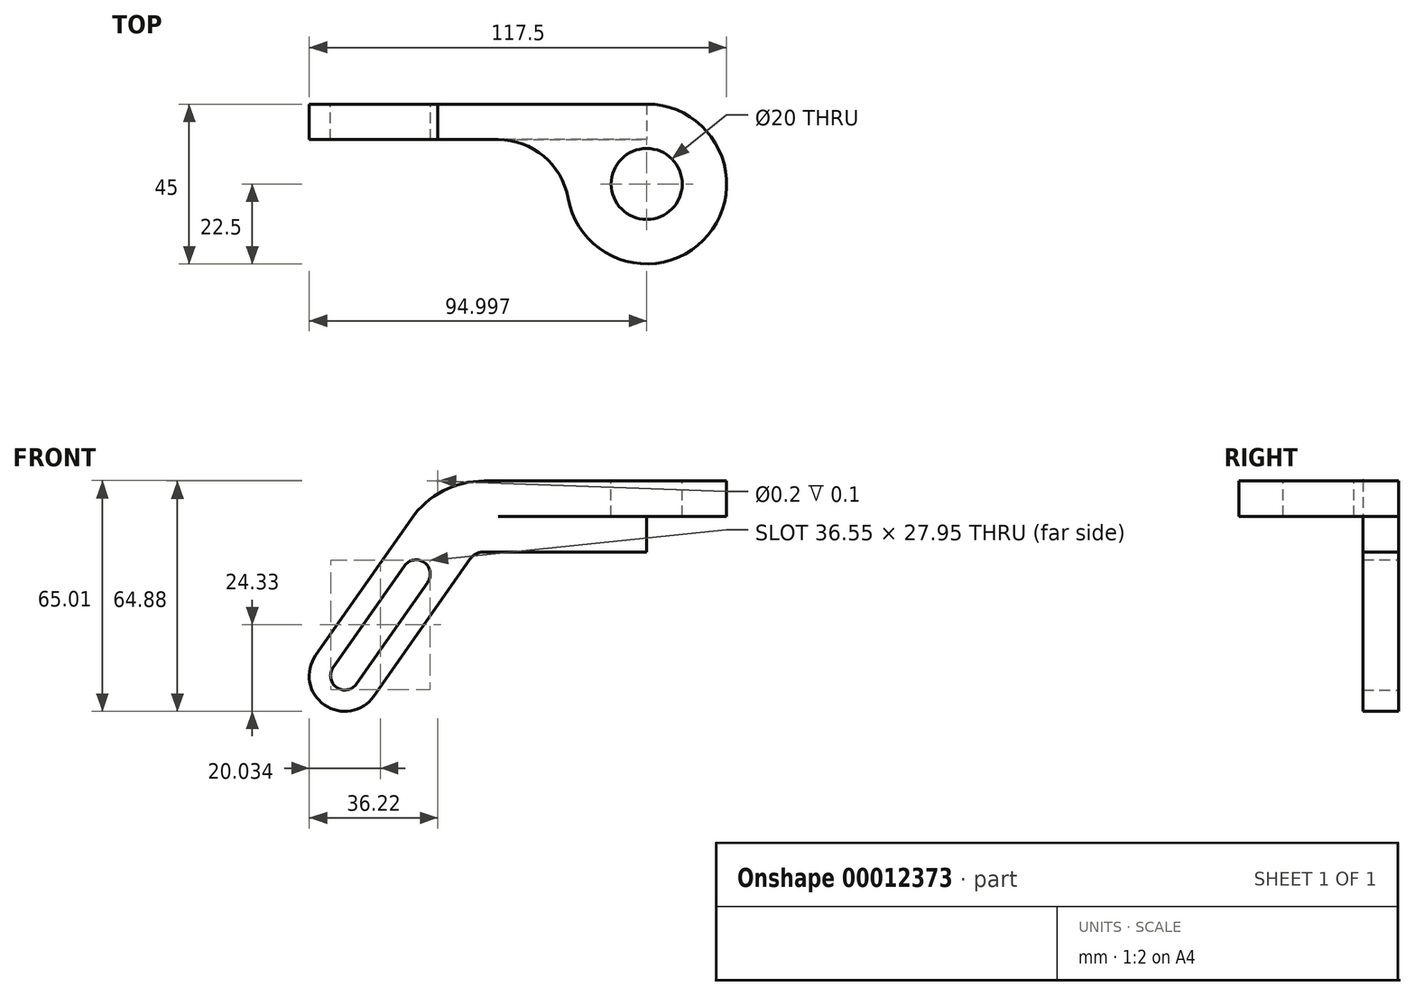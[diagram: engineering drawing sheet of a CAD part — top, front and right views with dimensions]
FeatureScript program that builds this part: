
annotation { "Feature Type Name" : "Feature", "Feature Type Description" : "" }
export const myFeature = defineFeature(function(context is Context, id is Id, definition is map)
    precondition{}
    {
        {
            var Q0;
            Q0=qCreatedBy(makeId("Front.planeOp"),FACE);
            var sketch = newSketch(context, id + "F0", { "sketchPlane" : qUnion([Q0])});
            skLineSegment(sketch, "E0", {"start": v(13.01, 0) * mm, "end": v(58.78, 0) * mm});
            skLineSegment(sketch, "E1", {"start": v(-7.46, -10.66) * mm, "end": v(-34.41, -49.15) * mm});
            skLineSegment(sketch, "E2.0", {"start": v(8.92, -22.13) * mm, "end": v(-18.03, -60.62) * mm});
            skArc(sketch, "E3", {"start": v(-18.03, -60.62) * mm, "mid": v(-31.96, -63.08) * mm, "end": v(-34.41, -49.15) * mm});
            skLineSegment(sketch, "E4.0", {"start": v(13.01, -20) * mm, "end": v(58.78, -20) * mm});
            skLineSegment(sketch, "E5", {"start": v(58.78, 0) * mm, "end": v(58.78, -20) * mm});
            skPoint(sketch, "E6.visualSharp", {"position": v(0, 0) * mm});
            skArc(sketch, "E6.filletArc", {"start": v(13.01, 0) * mm, "mid": v(1.47, -2.82) * mm, "end": v(-7.46, -10.66) * mm});
            skArc(sketch, "E7.filletArc", {"start": v(13.01, -20) * mm, "mid": v(10.7, -20.56) * mm, "end": v(8.92, -22.13) * mm});
            skLineSegment(sketch, "E8", {"start": v(0, 0) * mm, "end": v(-4.4, -6.28) * mm, "construction": true});
            skLineSegment(sketch, "E9", {"start": v(0, 0) * mm, "end": v(6.9, 0) * mm, "construction": true});
            skCircle(sketch, "E10", {"center": v(0, 0) * mm, "radius": 0 * mm});
            skSolve(sketch);
        }
        {
            var Q0;
            Q0 = qSketchRegion(id + "F0", true);
            extrude(context, id + "F1", {"entities" : qUnion([Q0]), "depth" : 10 * mm});
        }
        {
            var Q0;
            Q0=makeQuery(id+"F1.opExtrude","SWEPT_FACE",FACE,{"disambiguationData":[OSD([sQuery(id+"F0.wireOp",EDGE,"E0")])]});
            var sketch = newSketch(context, id + "F2", { "sketchPlane" : qUnion([Q0])});
            skCircle(sketch, "E11", {"center": v(58.78, -22.5) * mm, "radius": 22.5 * mm});
            skSolve(sketch);
        }
        {
            var Q0;
            Q0 = qSketchRegion(id + "F2", true);
            extrude(context, id + "F3", {"entities" : qUnion([Q0]), "operationType" : NewBodyOperationType.ADD, "oppositeDirection" : true, "depth" : 10 * mm});
        }
        {
            var Q0;
            Q0=makeQuery(id+"F3.boolean.opBoolean","INTERSECT",EDGE,{"derivedFrom":[makeQuery(id+"F1.opExtrude","CAP_FACE",FACE,{"disambiguationData":[OSD([sQuery(id+"F0.wireOp",EDGE,"E0"),sQuery(id+"F0.wireOp",EDGE,"E1"),sQuery(id+"F0.wireOp",EDGE,"E2.0"),sQuery(id+"F0.wireOp",EDGE,"E3"),sQuery(id+"F0.wireOp",EDGE,"E4.0"),sQuery(id+"F0.wireOp",EDGE,"E5"),sQuery(id+"F0.wireOp",EDGE,"E6.filletArc"),sQuery(id+"F0.wireOp",EDGE,"E7.filletArc")])],"isStart":false}),makeQuery(id+"F3.opExtrude","SWEPT_FACE",FACE,{"disambiguationData":[OSD([sQuery(id+"F2.wireOp",EDGE,"E11")])]})]});
            fillet(context, id + "F4", {"entities" : qUnion([Q0]), "radius" : 20 * mm, "tangentPropagation" : true, "allowEdgeOverflow" : false});
        }
        {
            var Q0;
            Q0=makeQuery(id+"F1.opExtrude","CAP_FACE",FACE,{"disambiguationData":[OSD([sQuery(id+"F0.wireOp",EDGE,"E0"),sQuery(id+"F0.wireOp",EDGE,"E1"),sQuery(id+"F0.wireOp",EDGE,"E2.0"),sQuery(id+"F0.wireOp",EDGE,"E3"),sQuery(id+"F0.wireOp",EDGE,"E4.0"),sQuery(id+"F0.wireOp",EDGE,"E5"),sQuery(id+"F0.wireOp",EDGE,"E6.filletArc"),sQuery(id+"F0.wireOp",EDGE,"E7.filletArc")])],"isStart":true});
            var sketch = newSketch(context, id + "F5", { "sketchPlane" : qUnion([Q0])});
            skArc(sketch, "E12", {"start": v(22.95, -57.18) * mm, "mid": v(28.52, -58.16) * mm, "end": v(29.5, -52.6) * mm});
            skLineSegment(sketch, "E13", {"start": v(26.22, -54.88) * mm, "end": v(2.44, -20.92) * mm, "construction": true});
            skArc(sketch, "E14", {"start": v(9.42, -23.92) * mm, "mid": v(3.85, -22.94) * mm, "end": v(2.87, -28.5) * mm});
            skLineSegment(sketch, "E15", {"start": v(22.95, -57.18) * mm, "end": v(2.87, -28.5) * mm});
            skLineSegment(sketch, "E16.0", {"start": v(29.5, -52.6) * mm, "end": v(9.42, -23.92) * mm});
            skSolve(sketch);
        }
        {
            var Q0;
            Q0 = qSketchRegion(id + "F5", true);
            extrude(context, id + "F6", {"entities" : qUnion([Q0]), "operationType" : NewBodyOperationType.REMOVE, "endBound" : BoundingType.THROUGH_ALL, "oppositeDirection" : true, "depth" : 25 * mm});
        }
        {
            var Q0;
            Q0=makeQuery(id+"F3.boolean.opBoolean","MERGE",FACE,{"derivedFrom":[makeQuery(id+"F1.opExtrude","SWEPT_FACE",FACE,{"disambiguationData":[OSD([sQuery(id+"F0.wireOp",EDGE,"E0")])]}),makeQuery(id+"F3.opExtrude","CAP_FACE",FACE,{"disambiguationData":[OSD([sQuery(id+"F2.wireOp",EDGE,"E11")])],"isStart":true})]});
            var sketch = newSketch(context, id + "F7", { "sketchPlane" : qUnion([Q0])});
            skCircle(sketch, "E17", {"center": v(58.78, -22.5) * mm, "radius": 10 * mm});
            skSolve(sketch);
        }
        {
            var Q0;
            Q0 = qSketchRegion(id + "F7", true);
            extrude(context, id + "F8", {"entities" : qUnion([Q0]), "operationType" : NewBodyOperationType.REMOVE, "endBound" : BoundingType.THROUGH_ALL, "oppositeDirection" : true, "depth" : 25 * mm});
        }
        {
            var Q0;
            Q0=makeQuery(id+"F1.opExtrude","CAP_FACE",FACE,{"disambiguationData":[OSD([sQuery(id+"F0.wireOp",EDGE,"E0"),sQuery(id+"F0.wireOp",EDGE,"E1"),sQuery(id+"F0.wireOp",EDGE,"E2.0"),sQuery(id+"F0.wireOp",EDGE,"E3"),sQuery(id+"F0.wireOp",EDGE,"E4.0"),sQuery(id+"F0.wireOp",EDGE,"E5"),sQuery(id+"F0.wireOp",EDGE,"E6.filletArc"),sQuery(id+"F0.wireOp",EDGE,"E7.filletArc")])],"isStart":false});
            var sketch = newSketch(context, id + "F9", { "sketchPlane" : qUnion([Q0])});
            skLineSegment(sketch, "E18", {"start": v(0, 0) * mm, "end": v(-3.64, -5.2) * mm});
            skLineSegment(sketch, "E19", {"start": v(0, 0) * mm, "end": v(5.28, 0) * mm});
            skPoint(sketch, "E20", {"position": v(0, 0) * mm});
            skCircle(sketch, "E21", {"center": v(0, 0) * mm, "radius": 0.12 * mm});
            skLineSegment(sketch, "E22", {"start": v(0, 0.12) * mm, "end": v(0, -0.12) * mm});
            skLineSegment(sketch, "E23", {"start": v(-0.12, 0) * mm, "end": v(0.12, 0) * mm});
            skCircle(sketch, "E24", {"center": v(0, 0) * mm, "radius": 0.1 * mm});
            skSolve(sketch);
        }
        {
            var Q0;
            Q0 = qSketchRegion(id + "F9", true);
            extrude(context, id + "F10", {"entities" : qUnion([Q0]), "oppositeDirection" : true, "depth" : .1 * mm});
        }
    });
